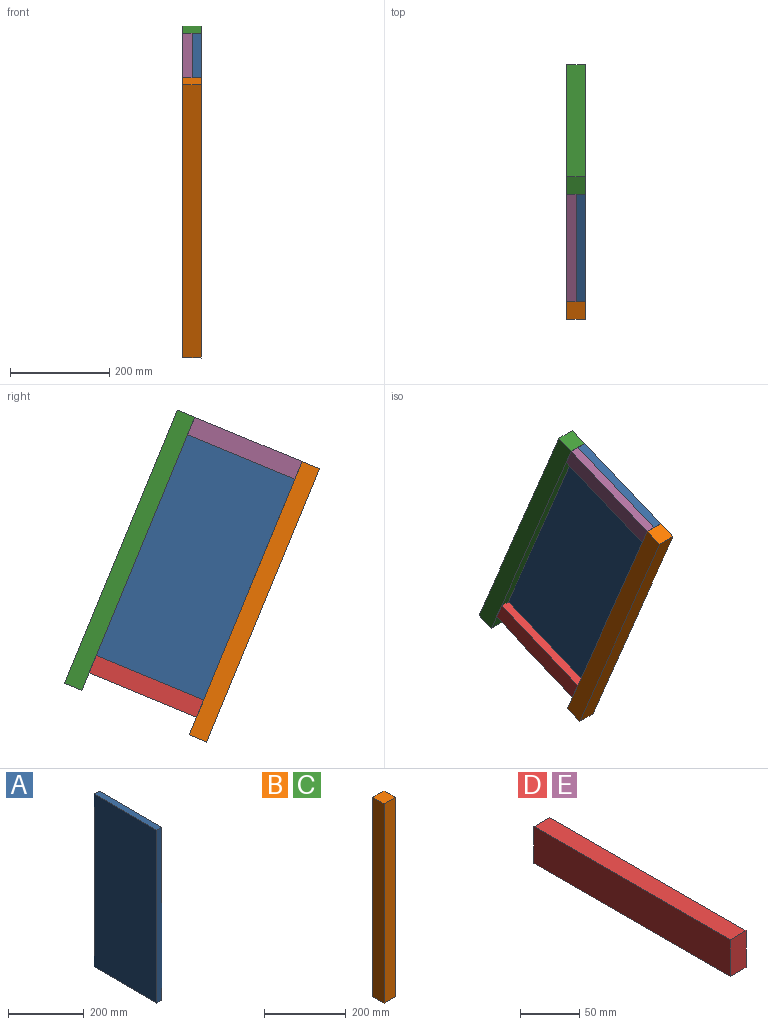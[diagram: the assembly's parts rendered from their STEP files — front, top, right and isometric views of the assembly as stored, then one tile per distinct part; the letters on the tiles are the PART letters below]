
ASSEMBLY  parts=5 mates=12
PART A: 6 faces, bbox 19.1x235x558.8 mm
  f0: plane 558.8x19.05mm, normal (0,1,0), area 10645.1mm2, adj f1,f3,f4,f5
  f1: plane 234.95x19.05mm, normal (0,0,1), area 4475.8mm2, adj f0,f2,f4,f5
  f2: plane 558.8x19.05mm, normal (0,-1,0), area 10645.1mm2, adj f1,f3,f4,f5
  f3: plane 234.95x19.05mm, normal (0,0,-1), area 4475.8mm2, adj f0,f2,f4,f5
  f4: plane 558.8x234.95mm, normal (1,0,0), area 131290.1mm2, adj f0,f1,f2,f3
  f5: plane 558.8x234.95mm, normal (-1,0,0), area 131290.1mm2, adj f0,f1,f2,f3
PART B: 6 faces, bbox 38.1x38.1x596.9 mm
  f0: plane 596.9x38.1mm, normal (0,-1,0), area 22741.9mm2, adj f1,f3,f4,f5
  f1: plane 596.9x38.1mm, normal (1,0,0), area 22741.9mm2, adj f0,f2,f4,f5
  f2: plane 596.9x38.1mm, normal (0,1,0), area 22741.9mm2, adj f1,f3,f4,f5
  f3: plane 596.9x38.1mm, normal (-1,0,0), area 22741.9mm2, adj f0,f2,f4,f5
  f4: plane 38.1x38.1mm, normal (0,0,1), area 1451.6mm2, adj f0,f1,f2,f3
  f5: plane 38.1x38.1mm, normal (0,0,-1), area 1451.6mm2, adj f0,f1,f2,f3
PART C: same geometry as B
PART D: 6 faces, bbox 19.1x235x38.1 mm
  f0: plane 234.95x19.05mm, normal (0,0,-1), area 4475.8mm2, adj f1,f3,f4,f5
  f1: plane 38.1x19.05mm, normal (0,1,0), area 725.8mm2, adj f0,f2,f4,f5
  f2: plane 234.95x19.05mm, normal (0,0,1), area 4475.8mm2, adj f1,f3,f4,f5
  f3: plane 38.1x19.05mm, normal (0,-1,0), area 725.8mm2, adj f0,f2,f4,f5
  f4: plane 234.95x38.1mm, normal (1,0,0), area 8951.6mm2, adj f0,f1,f2,f3
  f5: plane 234.95x38.1mm, normal (-1,0,0), area 8951.6mm2, adj f0,f1,f2,f3
PART E: same geometry as D
PLACE A rot(axis=(1,0,0),22.4deg) t=(69.73,234.32,-345.43)mm
PLACE B rot(axis=(0,0.19,-0.98),180deg) t=(69.73,229.38,-691)mm
PLACE C rot(axis=(0,0.19,-0.98),180deg) t=(69.73,481.74,-586.73)mm
PLACE D rot(axis=(1,0,0),22.4deg) t=(50.68,333.73,-586.05)mm
PLACE E rot(axis=(1,0,0),22.4deg) t=(50.68,134.91,-104.8)mm
MATE planar E.f4 <-> A.f5  axis (1,0,0) through (69.73,134.91,-104.8)mm
MATE planar D.f0 <-> A.f3  axis (0,0.38,-0.92) through (60.2,341.01,-603.65)mm
MATE planar A.f4 <-> C.f3  axis (1,0,0) through (88.78,234.32,-345.43)mm
MATE planar C.f2 <-> E.f1  axis (0,-0.92,-0.38) through (69.73,236.2,-42.34)mm
MATE planar A.f4 <-> B.f3  axis (1,0,0) through (88.78,234.32,-345.43)mm
MATE planar C.f2 <-> A.f0  axis (0,-0.92,-0.38) through (69.73,350.17,-318.17)mm
MATE planar B.f4 <-> C.f4  axis (0,-0.38,0.92) through (69.73,1.45,-139.33)mm
MATE planar A.f1 <-> C.f4  axis (0,-0.38,0.92) through (88.78,127.63,-87.2)mm
MATE planar A.f1 <-> E.f2  axis (0,-0.38,0.92) through (79.25,127.63,-87.2)mm
MATE planar A.f5 <-> D.f4  axis (-1,0,0) through (69.73,234.32,-345.43)mm
MATE planar B.f0 <-> A.f2  axis (0,0.92,0.38) through (88.78,19.06,-132.05)mm
MATE planar D.f3 <-> B.f0  axis (0,-0.92,-0.38) through (60.2,225.16,-630.91)mm
